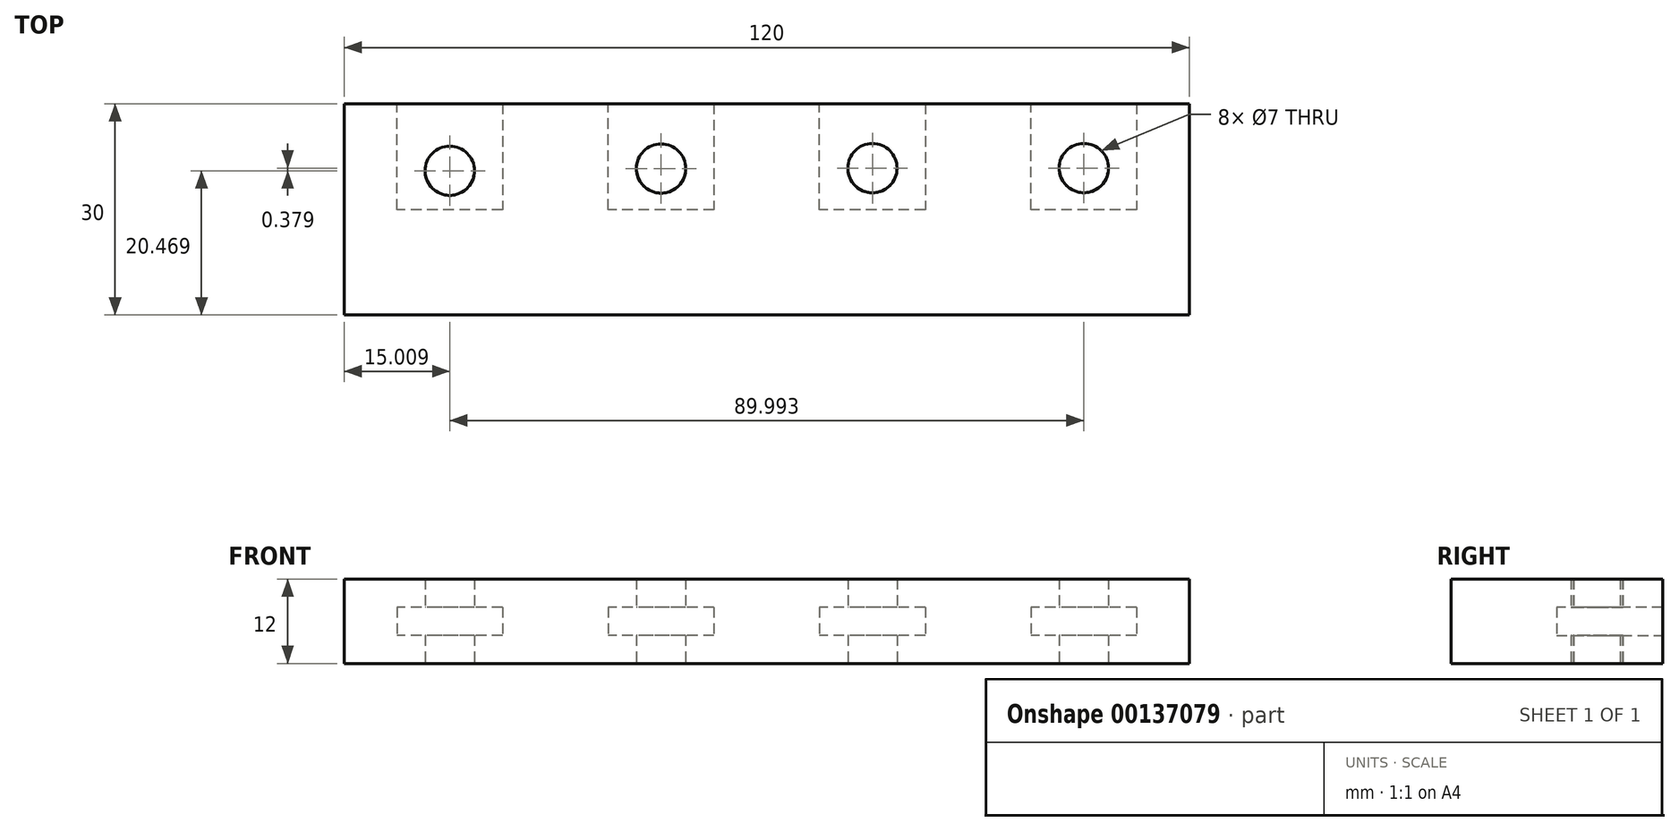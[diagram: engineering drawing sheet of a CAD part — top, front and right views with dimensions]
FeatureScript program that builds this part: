
annotation { "Feature Type Name" : "Feature", "Feature Type Description" : "" }
export const myFeature = defineFeature(function(context is Context, id is Id, definition is map)
    precondition{}
    {
        {
            var Q0;
            Q0=qCreatedBy(makeId("Top.planeOp"),FACE);
            var sketch = newSketch(context, id + "F0", { "sketchPlane" : qUnion([Q0])});
            skLineSegment(sketch, "E0", {"start": v(-87.75, 23.07) * mm, "end": v(-87.75, -6.93) * mm});
            skLineSegment(sketch, "E1", {"start": v(-87.75, -6.93) * mm, "end": v(30.24, -6.93) * mm});
            skLineSegment(sketch, "E2", {"start": v(30.24, -6.93) * mm, "end": v(30.24, 23.07) * mm});
            skCircle(sketch, "E3", {"center": v(-74.75, 13.54) * mm, "radius": 3.5 * mm});
            skCircle(sketch, "E4", {"center": v(-44.76, 13.86) * mm, "radius": 3.5 * mm});
            skCircle(sketch, "E5", {"center": v(-14.76, 13.9) * mm, "radius": 3.5 * mm});
            skCircle(sketch, "E6", {"center": v(15.24, 13.92) * mm, "radius": 3.5 * mm});
            skLineSegment(sketch, "E7", {"start": v(-87.75, 23.07) * mm, "end": v(-87.75, 19.07) * mm});
            skLineSegment(sketch, "E8", {"start": v(-87.75, 19.07) * mm, "end": v(-87.75, 17.07) * mm});
            skLineSegment(sketch, "E9", {"start": v(-74.75, 23.07) * mm, "end": v(-74.75, -6.93) * mm});
            skLineSegment(sketch, "E10", {"start": v(30.24, 23.07) * mm, "end": v(-74.75, 23.07) * mm});
            skLineSegment(sketch, "E11", {"start": v(-87.75, 23.07) * mm, "end": v(-74.75, 23.07) * mm});
            skLineSegment(sketch, "E12", {"start": v(-87.75, 23.07) * mm, "end": v(-89.76, 23.07) * mm});
            skLineSegment(sketch, "E13", {"start": v(-89.76, 23.07) * mm, "end": v(-89.76, -6.93) * mm});
            skLineSegment(sketch, "E14", {"start": v(-89.76, -6.93) * mm, "end": v(-87.75, -6.93) * mm});
            skSolve(sketch);
        }
        {
            var Q0;
            Q0 = qSketchRegion(id + "F0", true);
            extrude(context, id + "F1", {"entities" : qUnion([Q0]), "depth" : 4 * mm});
        }
        {
            var Q0;
            Q0=makeQuery(id+"F1.opExtrude","CAP_FACE",FACE,{"disambiguationData":[OSD([sQuery(id+"F0.wireOp",EDGE,"E0"),sQuery(id+"F0.wireOp",EDGE,"E1"),sQuery(id+"F0.wireOp",EDGE,"E2"),sQuery(id+"F0.wireOp",EDGE,"E3"),sQuery(id+"F0.wireOp",EDGE,"E4"),sQuery(id+"F0.wireOp",EDGE,"E5"),sQuery(id+"F0.wireOp",EDGE,"E6"),sQuery(id+"F0.wireOp",EDGE,"E7"),sQuery(id+"F0.wireOp",EDGE,"E8"),sQuery(id+"F0.wireOp",EDGE,"E10"),sQuery(id+"F0.wireOp",EDGE,"E11")])],"isStart":false});
            var sketch = newSketch(context, id + "F2", { "sketchPlane" : qUnion([Q0])});
            skLineSegment(sketch, "E15", {"start": v(30.23, 23.07) * mm, "end": v(30.24, -6.93) * mm});
            skLineSegment(sketch, "E16", {"start": v(30.24, -6.93) * mm, "end": v(30.24, -6.93) * mm});
            skLineSegment(sketch, "E17", {"start": v(30.24, -6.93) * mm, "end": v(30.24, 23.07) * mm});
            skLineSegment(sketch, "E18", {"start": v(30.24, 23.07) * mm, "end": v(22.73, 23.07) * mm});
            skLineSegment(sketch, "E19", {"start": v(22.73, 23.07) * mm, "end": v(22.73, 8.01) * mm});
            skLineSegment(sketch, "E20", {"start": v(22.73, 8.01) * mm, "end": v(7.73, 8.01) * mm});
            skLineSegment(sketch, "E21", {"start": v(7.73, 8.01) * mm, "end": v(7.73, 23.07) * mm});
            skLineSegment(sketch, "E22", {"start": v(7.73, 23.07) * mm, "end": v(-7.27, 23.07) * mm});
            skLineSegment(sketch, "E23", {"start": v(-7.27, 23.07) * mm, "end": v(-7.27, 8.01) * mm});
            skLineSegment(sketch, "E24", {"start": v(-7.27, 8.01) * mm, "end": v(-22.27, 8.01) * mm});
            skLineSegment(sketch, "E25", {"start": v(-22.27, 8.01) * mm, "end": v(-22.27, 23.07) * mm});
            skLineSegment(sketch, "E26", {"start": v(-22.27, 23.07) * mm, "end": v(-37.27, 23.07) * mm});
            skLineSegment(sketch, "E27", {"start": v(-37.27, 23.07) * mm, "end": v(-37.27, 8.01) * mm});
            skLineSegment(sketch, "E28", {"start": v(-37.27, 8.01) * mm, "end": v(-52.27, 8.01) * mm});
            skLineSegment(sketch, "E29", {"start": v(-52.27, 8.01) * mm, "end": v(-52.27, 23.07) * mm});
            skLineSegment(sketch, "E30", {"start": v(-52.27, 23.07) * mm, "end": v(-67.27, 23.07) * mm});
            skLineSegment(sketch, "E31", {"start": v(-67.27, 23.07) * mm, "end": v(-67.27, 8.01) * mm});
            skLineSegment(sketch, "E32", {"start": v(-67.27, 8.01) * mm, "end": v(-82.27, 8.01) * mm});
            skLineSegment(sketch, "E33", {"start": v(-82.27, 8.01) * mm, "end": v(-82.27, 23.07) * mm});
            skLineSegment(sketch, "E34", {"start": v(30.23, 23.07) * mm, "end": v(-82.27, 23.07) * mm});
            skLineSegment(sketch, "E35", {"start": v(-45.42, 68.46) * mm, "end": v(74.58, 68.46) * mm});
            skLineSegment(sketch, "E36", {"start": v(74.58, 68.46) * mm, "end": v(74.58, 98.46) * mm});
            skLineSegment(sketch, "E37", {"start": v(-37.93, 98.38) * mm, "end": v(-37.93, 88.38) * mm});
            skLineSegment(sketch, "E38", {"start": v(-22.93, 98.46) * mm, "end": v(-22.93, 88.46) * mm});
            skLineSegment(sketch, "E39", {"start": v(-7.93, 98.46) * mm, "end": v(-7.93, 88.46) * mm});
            skLineSegment(sketch, "E40", {"start": v(7.07, 98.46) * mm, "end": v(7.07, 88.46) * mm});
            skLineSegment(sketch, "E41", {"start": v(22.07, 98.46) * mm, "end": v(22.08, 88.46) * mm});
            skLineSegment(sketch, "E42", {"start": v(37.08, 98.46) * mm, "end": v(37.08, 88.46) * mm});
            skLineSegment(sketch, "E43", {"start": v(52.08, 98.46) * mm, "end": v(52.08, 88.46) * mm});
            skLineSegment(sketch, "E44", {"start": v(67.08, 98.46) * mm, "end": v(67.08, 88.46) * mm});
            skLineSegment(sketch, "E45", {"start": v(-22.93, 98.46) * mm, "end": v(-7.93, 98.46) * mm});
            skLineSegment(sketch, "E46", {"start": v(7.07, 98.46) * mm, "end": v(22.07, 98.46) * mm});
            skLineSegment(sketch, "E47", {"start": v(37.08, 98.46) * mm, "end": v(52.08, 98.46) * mm});
            skLineSegment(sketch, "E48", {"start": v(67.08, 98.46) * mm, "end": v(74.58, 98.46) * mm});
            skLineSegment(sketch, "E49", {"start": v(-45.42, 83.4) * mm, "end": v(-45.42, 68.46) * mm});
            skLineSegment(sketch, "E50", {"start": v(-37.93, 88.38) * mm, "end": v(-37.9, 83.4) * mm});
            skLineSegment(sketch, "E51", {"start": v(-22.93, 88.46) * mm, "end": v(-22.9, 83.4) * mm});
            skLineSegment(sketch, "E52", {"start": v(-7.93, 88.46) * mm, "end": v(-7.93, 83.4) * mm});
            skLineSegment(sketch, "E53", {"start": v(7.07, 88.46) * mm, "end": v(7.07, 83.4) * mm});
            skLineSegment(sketch, "E54", {"start": v(22.08, 88.46) * mm, "end": v(22.08, 83.4) * mm});
            skLineSegment(sketch, "E55", {"start": v(37.08, 88.46) * mm, "end": v(37.08, 83.4) * mm});
            skLineSegment(sketch, "E56", {"start": v(52.08, 88.46) * mm, "end": v(52.08, 83.4) * mm});
            skLineSegment(sketch, "E57", {"start": v(67.08, 88.46) * mm, "end": v(67.08, 83.4) * mm});
            skLineSegment(sketch, "E58", {"start": v(-37.9, 83.4) * mm, "end": v(-22.9, 83.4) * mm});
            skLineSegment(sketch, "E59", {"start": v(-7.93, 83.4) * mm, "end": v(7.07, 83.4) * mm});
            skLineSegment(sketch, "E60", {"start": v(22.08, 83.4) * mm, "end": v(37.08, 83.4) * mm});
            skLineSegment(sketch, "E61", {"start": v(52.08, 83.4) * mm, "end": v(67.08, 83.4) * mm});
            skLineSegment(sketch, "E62", {"start": v(-45.42, 68.46) * mm, "end": v(-45.42, 69.79) * mm});
            skLineSegment(sketch, "E63", {"start": v(-45.42, 98.46) * mm, "end": v(-45.42, 68.46) * mm});
            skLineSegment(sketch, "E64", {"start": v(-45.42, 98.46) * mm, "end": v(-37.93, 98.38) * mm});
            skLineSegment(sketch, "E65", {"start": v(30.24, -6.93) * mm, "end": v(30.23, 23.07) * mm});
            skLineSegment(sketch, "E66", {"start": v(30.24, 23.07) * mm, "end": v(30.24, -6.93) * mm});
            skLineSegment(sketch, "E67", {"start": v(-82.27, 23.07) * mm, "end": v(-89.76, 23.07) * mm});
            skLineSegment(sketch, "E68", {"start": v(-89.76, 23.07) * mm, "end": v(-89.76, -6.93) * mm});
            skLineSegment(sketch, "E69", {"start": v(-89.76, -6.93) * mm, "end": v(30.24, -6.93) * mm});
            skSolve(sketch);
        }
        {
            var Q0;
            Q0=makeQuery(id+"F2.imprint","IMPRINT",FACE,{"disambiguationData":[TD([[makeQuery(id+"F2.imprint","IMPRINT",EDGE,{"derivedFrom":sQuery(id+"F2.wireOp",EDGE,"E18")}),1.0]])]});
            var Q1;
            {var subQ2=sQuery(id+"F2.wireOp",EDGE,"E19");Q1=makeQuery(id+"F2.imprint","IMPRINT",FACE,{"disambiguationData":[TD([[makeQuery(id+"F2.imprint","IMPRINT",EDGE,{"derivedFrom":subQ2}),1.0]])]});}
            extrude(context, id + "F3", {"entities" : qUnion([Q0, Q1]), "operationType" : NewBodyOperationType.ADD, "depth" : 4 * mm});
        }
        {
            var Q0;
            Q0=makeQuery(id+"F3.opExtrude","CAP_FACE",FACE,{"disambiguationData":[OSD([sQuery(id+"F2.wireOp",EDGE,"E18"),sQuery(id+"F2.wireOp",EDGE,"E19"),sQuery(id+"F2.wireOp",EDGE,"E20"),sQuery(id+"F2.wireOp",EDGE,"E21"),sQuery(id+"F2.wireOp",EDGE,"E23"),sQuery(id+"F2.wireOp",EDGE,"E24"),sQuery(id+"F2.wireOp",EDGE,"E25"),sQuery(id+"F2.wireOp",EDGE,"E27"),sQuery(id+"F2.wireOp",EDGE,"E28"),sQuery(id+"F2.wireOp",EDGE,"E29"),sQuery(id+"F2.wireOp",EDGE,"E31"),sQuery(id+"F2.wireOp",EDGE,"E32"),sQuery(id+"F2.wireOp",EDGE,"E33"),sQuery(id+"F2.wireOp",EDGE,"E34"),sQuery(id+"F2.wireOp",EDGE,"E66"),sQuery(id+"F2.wireOp",EDGE,"E67"),sQuery(id+"F2.wireOp",EDGE,"E68"),sQuery(id+"F2.wireOp",EDGE,"E69")])],"isStart":false});
            var sketch = newSketch(context, id + "F4", { "sketchPlane" : qUnion([Q0])});
            skCircle(sketch, "E70", {"center": v(-74.75, 13.54) * mm, "radius": 3.5 * mm});
            skCircle(sketch, "E71", {"center": v(-44.76, 13.86) * mm, "radius": 3.5 * mm});
            skCircle(sketch, "E72", {"center": v(-14.76, 13.9) * mm, "radius": 3.5 * mm});
            skCircle(sketch, "E73", {"center": v(15.24, 13.92) * mm, "radius": 3.5 * mm});
            skLineSegment(sketch, "E74", {"start": v(-89.76, 23.07) * mm, "end": v(-89.76, -6.93) * mm});
            skLineSegment(sketch, "E75", {"start": v(-89.76, -6.93) * mm, "end": v(30.24, -6.93) * mm});
            skLineSegment(sketch, "E76", {"start": v(30.24, -6.93) * mm, "end": v(30.24, 23.07) * mm});
            skLineSegment(sketch, "E77", {"start": v(30.24, 23.07) * mm, "end": v(-89.76, 23.07) * mm});
            skSolve(sketch);
        }
        {
            var Q0;
            {var subQ2=makeQuery(id+"F3.opExtrude","CAP_EDGE",EDGE,{"disambiguationData":[OSD([sQuery(id+"F2.wireOp",EDGE,"E20")])],"isStart":false});Q0=makeQuery(id+"F4.imprint","IMPRINT",FACE,{"disambiguationData":[TD([[makeQuery(id+"F4.imprint","IMPRINT",EDGE,{"derivedFrom":subQ2}),1.0]])]});}
            var Q1;
            {var subQ6=sQuery(id+"F4.wireOp",EDGE,"eceb6e51-60e2-4bcd-b1b5-924ca2696937");Q1=makeQuery(id+"F4.imprint","IMPRINT",FACE,{"disambiguationData":[TD([[makeQuery(id+"F4.imprint","IMPRINT",EDGE,{"derivedFrom":subQ6}),1.0]])]});}
            var Q2;
            Q2=makeQuery(id+"F4.imprint","IMPRINT",FACE,{"disambiguationData":[TD([[makeQuery(id+"F4.imprint","IMPRINT",EDGE,{"derivedFrom":sQuery(id+"F4.wireOp",EDGE,"eceb6e51-60e2-4bcd-b1b5-924ca2696937")}),-1.0]])]});
            var Q3;
            Q3=makeQuery(id+"F4.imprint","IMPRINT",FACE,{"disambiguationData":[TD([[makeQuery(id+"F4.imprint","IMPRINT",EDGE,{"derivedFrom":sQuery(id+"F4.wireOp",EDGE,"E71")}),-1.0]])]});
            var Q4;
            {var subQ1=sQuery(id+"F4.wireOp",EDGE,"58a35af4-dfca-4147-95fc-391195326d5b");var subQ5=sQuery(id+"F4.wireOp",EDGE,"E70");var subQ9=makeQuery(id+"F4.imprint","INTERSECT",VERTEX,{"disambiguationData":[OD(0.0)],"derivedFrom":[subQ5,subQ1]});Q4=makeQuery(id+"F4.imprint","IMPRINT",FACE,{"disambiguationData":[TD([[makeQuery(id+"F4.imprint","IMPRINT",EDGE,{"disambiguationData":[TD([[subQ9,-1.0]])],"derivedFrom":subQ5}),-1.0]])]});}
            var Q5;
            {var subQ1=sQuery(id+"F4.wireOp",EDGE,"58a35af4-dfca-4147-95fc-391195326d5b");var subQ5=sQuery(id+"F4.wireOp",EDGE,"E70");var subQ9=makeQuery(id+"F4.imprint","INTERSECT",VERTEX,{"disambiguationData":[OD(0.0)],"derivedFrom":[subQ5,subQ1]});Q5=makeQuery(id+"F4.imprint","IMPRINT",FACE,{"disambiguationData":[TD([[makeQuery(id+"F4.imprint","IMPRINT",EDGE,{"disambiguationData":[TD([[subQ9,1.0]])],"derivedFrom":subQ5}),-1.0]])]});}
            var Q6;
            Q6=makeQuery(id+"F4.imprint","IMPRINT",FACE,{"disambiguationData":[TD([[makeQuery(id+"F4.imprint","IMPRINT",EDGE,{"derivedFrom":sQuery(id+"F4.wireOp",EDGE,"E72")}),-1.0]])]});
            var Q7;
            Q7=makeQuery(id+"F4.imprint","IMPRINT",FACE,{"disambiguationData":[TD([[makeQuery(id+"F4.imprint","IMPRINT",EDGE,{"derivedFrom":sQuery(id+"F4.wireOp",EDGE,"E73")}),-1.0]])]});
            var Q8;
            Q8=makeQuery(id+"F4.imprint","IMPRINT",FACE,{"disambiguationData":[TD([[makeQuery(id+"F4.imprint","IMPRINT",EDGE,{"derivedFrom":sQuery(id+"F4.wireOp",EDGE,"E70")}),-1.0]])]});
            extrude(context, id + "F5", {"entities" : qUnion([Q0, Q1, Q2, Q3, Q4, Q5, Q6, Q7, Q8]), "operationType" : NewBodyOperationType.ADD, "depth" : 4 * mm});
        }
    });
